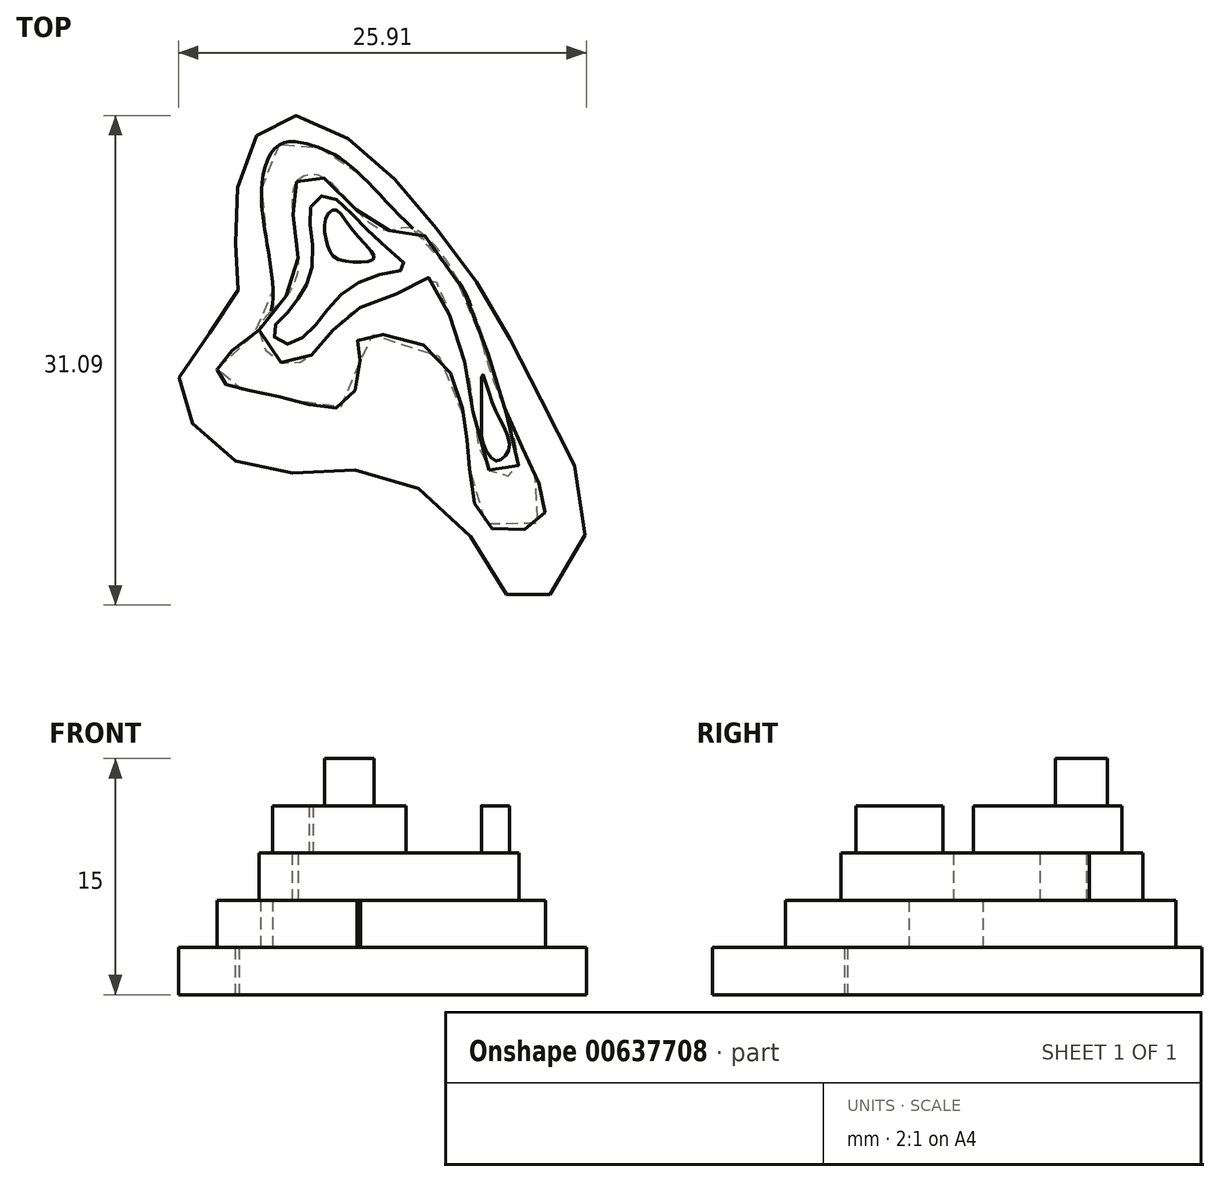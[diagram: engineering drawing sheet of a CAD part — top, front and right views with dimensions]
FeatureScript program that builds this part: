
annotation { "Feature Type Name" : "Feature", "Feature Type Description" : "" }
export const myFeature = defineFeature(function(context is Context, id is Id, definition is map)
    precondition{}
    {
        {
            var Q0;
            Q0=qCreatedBy(makeId("Top.planeOp"),FACE);
            var sketch = newSketch(context, id + "F0", { "sketchPlane" : qUnion([Q0])});
            skFitSpline(sketch, "E0", {"points": [v(-9.02, 21.1) * mm, v(-4.33, 16.54) * mm, v(0, 10.63) * mm, v(3.57, 3.91) * mm, v(6.02, -4.11) * mm, v(2.15, -8.53) * mm, v(-1.72, -3.5) * mm, v(-8.26, 0) * mm, v(-14.49, 0) * mm, v(-18.93, 3.03) * mm, v(-19.51, 6.57) * mm, v(-16.28, 10.61) * mm, v(-16.11, 14.1) * mm, v(-15.76, 19.14) * mm, v(-13.42, 22.43) * mm, v(-9.02, 21.1) * mm]});
            skSolve(sketch);
        }
        {
            var Q0;
            Q0 = qSketchRegion(id + "F0", true);
            var Q1;
            Q1 = qSketchRegion(id + "F2", true);
            extrude(context, id + "F1", {"entities" : qUnion([Q0, Q1]), "depth" : 3 * mm, "offsetDistance" : 25 * mm});
        }
        {
            var Q0;
            Q0=makeQuery(id+"F1.opExtrude","CAP_FACE",FACE,{"disambiguationData":[OSD([sQuery(id+"F0.wireOp",EDGE,"E0")])],"isStart":false});
            var sketch = newSketch(context, id + "F2", { "sketchPlane" : qUnion([Q0])});
            skFitSpline(sketch, "E1", {"points": [v(-13.38, 20.69) * mm, v(-14.46, 18.37) * mm, v(-14.27, 15.1) * mm, v(-13.8, 11.97) * mm, v(-14.38, 9.21) * mm, v(-17.16, 6.89) * mm, v(-17.09, 5.72) * mm, v(-15.26, 5.07) * mm, v(-11.93, 4.33) * mm, v(-9.29, 4.16) * mm, v(-8.23, 6.95) * mm, v(-8.32, 8.36) * mm, v(-3.87, 7.78) * mm, v(-1.63, 3.26) * mm, v(-1.27, 0) * mm, v(0, -3.6) * mm, v(3.27, -3.11) * mm, v(2.74, 0) * mm, v(0, 6.44) * mm, v(-1.75, 11.66) * mm, v(-5.69, 16.17) * mm, v(-9.08, 19.54) * mm, v(-11.31, 20.67) * mm, v(-13.38, 20.69) * mm]});
            skSolve(sketch);
        }
        {
            var Q0;
            Q0 = qSketchRegion(id + "F2", true);
            extrude(context, id + "F3", {"entities" : qUnion([Q0]), "operationType" : NewBodyOperationType.ADD, "depth" : 3 * mm, "offsetDistance" : 25 * mm});
        }
        {
            var Q0;
            Q0=makeQuery(id+"F3.opExtrude","CAP_FACE",FACE,{"disambiguationData":[OSD([sQuery(id+"F2.wireOp",EDGE,"E1")])],"isStart":false});
            var sketch = newSketch(context, id + "F4", { "sketchPlane" : qUnion([Q0])});
            skFitSpline(sketch, "E2", {"points": [v(-12.27, 18.35) * mm, v(-12.55, 16.73) * mm, v(-12.19, 13.8) * mm, v(-12.79, 11.27) * mm, v(-14.66, 8.92) * mm, v(-13.27, 6.87) * mm, v(-11.6, 7.12) * mm, v(-10.54, 8.21) * mm, v(-9.13, 9.75) * mm, v(-7.5, 10.7) * mm, v(-5.01, 11.64) * mm, v(-3.64, 12.2) * mm, v(-2.08, 8.25) * mm, v(-1.27, 5.58) * mm, v(0, 0) * mm, v(1.68, 0) * mm, v(0.89, 4.08) * mm, v(-1.2, 10.45) * mm, v(-4.9, 15.37) * mm, v(-6.73, 15.25) * mm, v(-9.1, 17.27) * mm, v(-11.08, 18.8) * mm, v(-12.27, 18.35) * mm]});
            skSolve(sketch);
        }
        {
            var Q0;
            Q0 = qSketchRegion(id + "F4", true);
            extrude(context, id + "F5", {"entities" : qUnion([Q0]), "operationType" : NewBodyOperationType.ADD, "depth" : 3 * mm, "offsetDistance" : 25 * mm});
        }
        {
            var Q0;
            Q0=makeQuery(id+"F5.opExtrude","CAP_FACE",FACE,{"disambiguationData":[OSD([sQuery(id+"F4.wireOp",EDGE,"E2")])],"isStart":false});
            var sketch = newSketch(context, id + "F6", { "sketchPlane" : qUnion([Q0])});
            skFitSpline(sketch, "E3", {"points": [v(-0.52, 3.43) * mm, v(-0.52, 2.5) * mm, v(-0.38, 1.57) * mm, v(0.37, 0.61) * mm, v(0.9, 0.84) * mm, v(1.25, 1.5) * mm, v(0.77, 3.01) * mm, v(0, 4.73) * mm, v(-0.47, 6.1) * mm, v(-0.52, 3.43) * mm]});
            skFitSpline(sketch, "E4", {"points": [v(-11.37, 16.72) * mm, v(-11.33, 14.96) * mm, v(-11.36, 12.54) * mm, v(-12.06, 11.12) * mm, v(-12.95, 9.91) * mm, v(-13.8, 8.88) * mm, v(-13.17, 8.08) * mm, v(-11.9, 8.43) * mm, v(-10.68, 9.75) * mm, v(-9.22, 11.37) * mm, v(-6.87, 12.49) * mm, v(-5.33, 12.91) * mm, v(-6.87, 14.43) * mm, v(-8.99, 16.55) * mm, v(-10.46, 17.48) * mm, v(-11.37, 16.72) * mm]});
            skSolve(sketch);
        }
        {
            var Q0;
            Q0 = qSketchRegion(id + "F6", true);
            extrude(context, id + "F7", {"entities" : qUnion([Q0]), "operationType" : NewBodyOperationType.ADD, "depth" : 3 * mm, "offsetDistance" : 25 * mm});
        }
        {
            var Q0;
            Q0=makeQuery(id+"F7.opExtrude","CAP_FACE",FACE,{"disambiguationData":[OSD([sQuery(id+"F6.wireOp",EDGE,"E4")])],"isStart":false});
            var sketch = newSketch(context, id + "F8", { "sketchPlane" : qUnion([Q0])});
            skFitSpline(sketch, "E5", {"points": [v(-10.45, 15.99) * mm, v(-10.36, 14.56) * mm, v(-9.85, 13.54) * mm, v(-8.2, 13.25) * mm, v(-7.35, 13.51) * mm, v(-8.72, 15.28) * mm, v(-9.85, 16.57) * mm, v(-10.45, 15.99) * mm]});
            skSolve(sketch);
        }
        {
            var Q0;
            Q0 = qSketchRegion(id + "F8", true);
            extrude(context, id + "F9", {"entities" : qUnion([Q0]), "operationType" : NewBodyOperationType.ADD, "depth" : 3 * mm, "offsetDistance" : 25 * mm});
        }
    });
